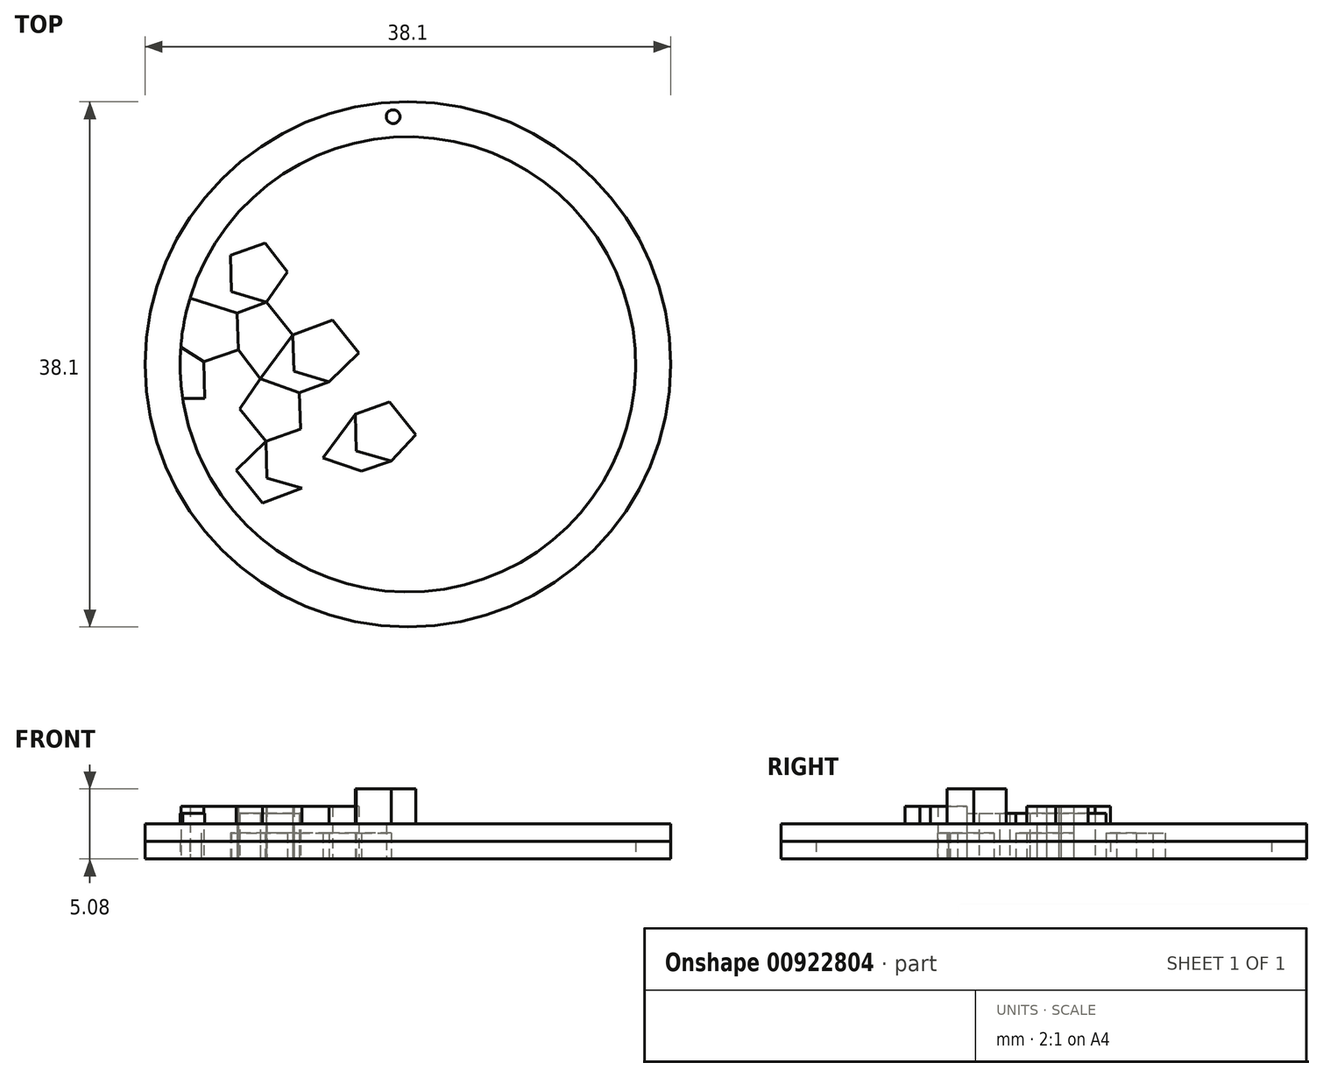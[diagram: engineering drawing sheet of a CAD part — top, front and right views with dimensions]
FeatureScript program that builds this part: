
annotation { "Feature Type Name" : "Feature", "Feature Type Description" : "" }
export const myFeature = defineFeature(function(context is Context, id is Id, definition is map)
    precondition{}
    {
        {
            var Q0;
            Q0=qCreatedBy(makeId("Top.planeOp"),FACE);
            var sketch = newSketch(context, id + "F0", { "sketchPlane" : qUnion([Q0])});
            skCircle(sketch, "E0", {"center": v(1.07, 1.9) * mm, "radius": 19.05 * mm});
            skPoint(sketch, "E0.first.point", {"position": v(-17.89, 0) * mm});
            skPoint(sketch, "E0.first.point.positionSnap0", {"position": v(-17.89, -0.57) * mm});
            skPoint(sketch, "E0.second.point", {"position": v(1.18, 20.95) * mm});
            skPoint(sketch, "E0.second.point.positionSnap0", {"position": v(1.18, 19.99) * mm});
            skPoint(sketch, "E0.third.point", {"position": v(19, -4.54) * mm});
            skCircle(sketch, "E1", {"center": v(1.07, 1.9) * mm, "radius": 16.51 * mm});
            skLineSegment(sketch, "E2.0", {"start": v(-11.37, -5.79) * mm, "end": v(-13.92, -5.03) * mm});
            skLineSegment(sketch, "E2.1", {"start": v(-13.92, -5.03) * mm, "end": v(-13.99, -2.38) * mm});
            skLineSegment(sketch, "E2.2", {"start": v(-13.99, -2.38) * mm, "end": v(-11.12, -1.32) * mm});
            skLineSegment(sketch, "E2.3", {"start": v(-11.23, 2.97) * mm, "end": v(-9.62, 0.87) * mm});
            skLineSegment(sketch, "E2.4", {"start": v(-9.22, -3.68) * mm, "end": v(-11.37, -5.79) * mm});
            skLineSegment(sketch, "E3.0", {"start": v(-9.22, -3.68) * mm, "end": v(-11.12, -1.32) * mm});
            skLineSegment(sketch, "E3.1", {"start": v(-11.23, 2.97) * mm, "end": v(-11.3, 5.63) * mm});
            skLineSegment(sketch, "E3.2", {"start": v(-11.3, 5.63) * mm, "end": v(-9.17, 6.41) * mm});
            skLineSegment(sketch, "E3.3", {"start": v(-9.17, 6.41) * mm, "end": v(-7.27, 4.05) * mm});
            skLineSegment(sketch, "E3.4", {"start": v(-7.27, 4.05) * mm, "end": v(-9.62, 0.87) * mm});
            skLineSegment(sketch, "E4.0", {"start": v(-11.12, -1.32) * mm, "end": v(-13.67, -0.57) * mm});
            skLineSegment(sketch, "E4.1", {"start": v(-13.67, -0.57) * mm, "end": v(-13.73, 2.09) * mm});
            skLineSegment(sketch, "E4.2", {"start": v(-13.73, 2.09) * mm, "end": v(-11.23, 2.97) * mm});
            skLineSegment(sketch, "E4.4", {"start": v(-9.62, 0.87) * mm, "end": v(-11.12, -1.32) * mm});
            skLineSegment(sketch, "E5.0", {"start": v(-9.62, 0.87) * mm, "end": v(-11.23, 2.97) * mm});
            skLineSegment(sketch, "E6.1.0.0", {"start": v(-4.7, -9.45) * mm, "end": v(-6.86, -11.55) * mm});
            skLineSegment(sketch, "E6.1.0.1", {"start": v(-6.86, -11.55) * mm, "end": v(-9.4, -10.8) * mm});
            skLineSegment(sketch, "E6.1.0.2", {"start": v(-9.4, -10.8) * mm, "end": v(-9.47, -8.15) * mm});
            skLineSegment(sketch, "E6.1.0.3", {"start": v(-9.47, -8.15) * mm, "end": v(-6.6, -7.09) * mm});
            skLineSegment(sketch, "E6.1.0.4", {"start": v(-4.7, -9.45) * mm, "end": v(-6.6, -7.09) * mm});
            skLineSegment(sketch, "E6.1.0.5", {"start": v(-5.1, -4.9) * mm, "end": v(-6.6, -7.09) * mm});
            skLineSegment(sketch, "E6.1.0.6", {"start": v(-6.6, -7.09) * mm, "end": v(-9.15, -6.33) * mm});
            skLineSegment(sketch, "E6.1.0.7", {"start": v(-9.15, -6.33) * mm, "end": v(-9.22, -3.68) * mm});
            skLineSegment(sketch, "E6.1.0.8", {"start": v(-9.22, -3.68) * mm, "end": v(-6.72, -2.8) * mm});
            skLineSegment(sketch, "E6.1.0.9", {"start": v(-5.1, -4.9) * mm, "end": v(-6.72, -2.8) * mm});
            skLineSegment(sketch, "E6.1.0.10", {"start": v(-6.72, -2.8) * mm, "end": v(-5.1, -4.9) * mm});
            skLineSegment(sketch, "E6.1.0.11", {"start": v(-2.75, -1.71) * mm, "end": v(-5.1, -4.9) * mm});
            skLineSegment(sketch, "E6.1.0.12", {"start": v(-4.66, 0.65) * mm, "end": v(-2.75, -1.71) * mm});
            skLineSegment(sketch, "E6.1.0.13", {"start": v(-6.79, -0.14) * mm, "end": v(-4.66, 0.65) * mm});
            skLineSegment(sketch, "E6.1.0.14", {"start": v(-6.72, -2.8) * mm, "end": v(-6.79, -0.14) * mm});
            skLineSegment(sketch, "E6.direction1", {"start": v(-13.92, -5.03) * mm, "end": v(-9.4, -10.8) * mm, "construction": true});
            skLineSegment(sketch, "E7", {"start": v(-11.37, -5.79) * mm, "end": v(-9.47, -8.15) * mm});
            skLineSegment(sketch, "E8", {"start": v(-9.62, 0.87) * mm, "end": v(-6.79, -0.14) * mm});
            skLineSegment(sketch, "E9.1.0.0", {"start": v(-4.66, 0.65) * mm, "end": v(-7.2, 1.4) * mm});
            skLineSegment(sketch, "E9.1.0.1", {"start": v(-7.2, 1.4) * mm, "end": v(-7.27, 4.05) * mm});
            skLineSegment(sketch, "E9.1.0.2", {"start": v(-7.27, 4.05) * mm, "end": v(-4.4, 5.11) * mm});
            skLineSegment(sketch, "E9.1.0.3", {"start": v(-2.5, 2.75) * mm, "end": v(-4.4, 5.11) * mm});
            skLineSegment(sketch, "E9.1.0.4", {"start": v(-2.5, 2.75) * mm, "end": v(-4.66, 0.65) * mm});
            skLineSegment(sketch, "E9.direction1", {"start": v(-9.4, -10.8) * mm, "end": v(-7.2, 1.4) * mm, "construction": true});
            skLineSegment(sketch, "E10.1.0.0", {"start": v(-2.68, -4.37) * mm, "end": v(-2.75, -1.71) * mm});
            skLineSegment(sketch, "E10.1.0.1", {"start": v(-0.14, -5.12) * mm, "end": v(-2.68, -4.37) * mm});
            skLineSegment(sketch, "E10.1.0.2", {"start": v(1.65, -3.19) * mm, "end": v(-0.14, -5.12) * mm});
            skLineSegment(sketch, "E10.1.0.3", {"start": v(-2.75, -1.71) * mm, "end": v(-0.25, -0.83) * mm});
            skLineSegment(sketch, "E10.1.0.4", {"start": v(1.65, -3.19) * mm, "end": v(-0.25, -0.83) * mm});
            skLineSegment(sketch, "E10.direction1", {"start": v(-9.4, -10.8) * mm, "end": v(-0.9, -7.3) * mm, "construction": true});
            skLineSegment(sketch, "E11.1.0.1", {"start": v(-7.67, 8.6) * mm, "end": v(-9.17, 6.41) * mm});
            skLineSegment(sketch, "E11.1.0.2", {"start": v(-7.67, 8.6) * mm, "end": v(-4.84, 7.67) * mm});
            skLineSegment(sketch, "E11.1.0.3", {"start": v(-4.4, 5.11) * mm, "end": v(-4.84, 7.67) * mm});
            skLineSegment(sketch, "E11.1.0.5", {"start": v(-9.17, 6.41) * mm, "end": v(-11.72, 7.17) * mm});
            skLineSegment(sketch, "E11.1.0.6", {"start": v(-11.72, 7.17) * mm, "end": v(-11.79, 9.82) * mm});
            skLineSegment(sketch, "E11.1.0.7", {"start": v(-11.79, 9.82) * mm, "end": v(-9.28, 10.7) * mm});
            skLineSegment(sketch, "E11.1.0.8", {"start": v(-7.67, 8.6) * mm, "end": v(-9.28, 10.7) * mm});
            skLineSegment(sketch, "E11.direction1", {"start": v(-9.22, -3.68) * mm, "end": v(-6.74, 4.77) * mm, "construction": true});
            skLineSegment(sketch, "E12.1.0.2", {"start": v(-5.1, -4.9) * mm, "end": v(-2.28, -5.83) * mm});
            skLineSegment(sketch, "E12.1.0.3", {"start": v(-2.2, -8.49) * mm, "end": v(-2.28, -5.83) * mm});
            skLineSegment(sketch, "E12.1.0.4", {"start": v(-4.7, -9.37) * mm, "end": v(-2.2, -8.49) * mm});
            skLineSegment(sketch, "E12.direction1", {"start": v(-9.22, -3.68) * mm, "end": v(15.78, -3.68) * mm, "construction": true});
            skLineSegment(sketch, "E13", {"start": v(-13.73, 2.09) * mm, "end": v(-15.4, 3.16) * mm});
            skLineSegment(sketch, "E14", {"start": v(-13.67, -0.57) * mm, "end": v(-15.26, -0.57) * mm});
            skLineSegment(sketch, "E15", {"start": v(-2.28, -5.83) * mm, "end": v(-0.14, -5.12) * mm});
            skLineSegment(sketch, "E16.direction1", {"start": v(-11.12, -1.32) * mm, "end": v(-15.9, 4.6) * mm, "construction": true});
            skLineSegment(sketch, "E17", {"start": v(-11.3, 5.63) * mm, "end": v(-14.73, 6.72) * mm});
            skLineSegment(sketch, "E18", {"start": v(-14.73, 6.72) * mm, "end": v(-11.79, 9.82) * mm});
            skLineSegment(sketch, "E19", {"start": v(-11.79, 9.82) * mm, "end": v(-13.19, 10.23) * mm});
            skSolve(sketch);
        }
        {
            var Q0;
            Q0 = qSketchRegion(id + "F0", true);
            extrude(context, id + "F1", {"entities" : qUnion([Q0]), "depth" : 2.54 * mm, "offsetDistance" : 25 * mm});
        }
        {
            var Q0;
            Q0=makeQuery(id+"F0.imprint","IMPRINT",FACE,{"disambiguationData":[TD([[makeQuery(id+"F0.imprint","IMPRINT",EDGE,{"derivedFrom":sQuery(id+"F0.wireOp",EDGE,"E9.1.0.0")}),-1.0]])]});
            var Q1;
            Q1=makeQuery(id+"F0.imprint","IMPRINT",FACE,{"disambiguationData":[TD([[makeQuery(id+"F0.imprint","IMPRINT",EDGE,{"derivedFrom":sQuery(id+"F0.wireOp",EDGE,"E3.1")}),1.0]])]});
            var Q2;
            Q2=makeQuery(id+"F0.imprint","IMPRINT",FACE,{"disambiguationData":[TD([[makeQuery(id+"F0.imprint","IMPRINT",EDGE,{"derivedFrom":sQuery(id+"F0.wireOp",EDGE,"E2.4")}),1.0]])]});
            extrude(context, id + "F2", {"entities" : qUnion([Q0, Q1, Q2]), "depth" : 3.81 * mm, "offsetDistance" : 25 * mm});
        }
        {
            var Q0;
            Q0=makeQuery(id+"F0.imprint","IMPRINT",FACE,{"disambiguationData":[TD([[makeQuery(id+"F0.imprint","IMPRINT",EDGE,{"derivedFrom":sQuery(id+"F0.wireOp",EDGE,"E3.4")}),1.0]])]});
            var Q1;
            Q1=makeQuery(id+"F0.imprint","IMPRINT",FACE,{"disambiguationData":[TD([[makeQuery(id+"F0.imprint","IMPRINT",EDGE,{"derivedFrom":sQuery(id+"F0.wireOp",EDGE,"E2.0")}),-1.0]])]});
            var Q2;
            {var subQ1=sQuery(id+"F0.wireOp",EDGE,"E11.1.0.1");Q2=makeQuery(id+"F0.imprint","IMPRINT",FACE,{"disambiguationData":[TD([[makeQuery(id+"F0.imprint","IMPRINT",EDGE,{"derivedFrom":subQ1}),-1.0]])]});}
            var Q3;
            Q3=makeQuery(id+"F0.imprint","IMPRINT",FACE,{"disambiguationData":[TD([[makeQuery(id+"F0.imprint","IMPRINT",EDGE,{"derivedFrom":sQuery(id+"F0.wireOp",EDGE,"E6.1.0.11")}),1.0]])]});
            extrude(context, id + "F3", {"entities" : qUnion([Q0, Q1, Q2, Q3]), "depth" : 1.9 * mm, "offsetDistance" : 25 * mm});
        }
        {
            var Q0;
            {var subQ1=sQuery(id+"F0.wireOp",EDGE,"E2.0");Q0=makeQuery(id+"F0.imprint","IMPRINT",FACE,{"disambiguationData":[TD([[makeQuery(id+"F0.imprint","IMPRINT",EDGE,{"derivedFrom":subQ1}),1.0]])]});}
            extrude(context, id + "F4", {"entities" : qUnion([Q0]), "depth" : 1.27 * mm, "offsetDistance" : 25 * mm});
        }
        {
            var Q0;
            Q0=makeQuery(id+"F0.imprint","IMPRINT",FACE,{"disambiguationData":[TD([[makeQuery(id+"F0.imprint","IMPRINT",EDGE,{"derivedFrom":sQuery(id+"F0.wireOp",EDGE,"E10.1.0.0")}),-1.0]])]});
            extrude(context, id + "F5", {"entities" : qUnion([Q0]), "depth" : 5.08 * mm, "offsetDistance" : 25 * mm});
        }
        {
            var Q0;
            Q0=makeQuery(id+"F0.imprint","IMPRINT",FACE,{"disambiguationData":[TD([[makeQuery(id+"F0.imprint","IMPRINT",EDGE,{"derivedFrom":sQuery(id+"F0.wireOp",EDGE,"E3.1")}),-1.0]])]});
            var Q1;
            Q1=makeQuery(id+"F0.imprint","IMPRINT",FACE,{"disambiguationData":[TD([[makeQuery(id+"F0.imprint","IMPRINT",EDGE,{"derivedFrom":sQuery(id+"F0.wireOp",EDGE,"E3.0")}),-1.0]])]});
            var Q2;
            Q2=makeQuery(id+"F0.imprint","IMPRINT",FACE,{"disambiguationData":[TD([[makeQuery(id+"F0.imprint","IMPRINT",EDGE,{"derivedFrom":sQuery(id+"F0.wireOp",EDGE,"E4.1")}),1.0]])]});
            extrude(context, id + "F6", {"entities" : qUnion([Q0, Q1, Q2]), "depth" : 3.3 * mm, "offsetDistance" : 25 * mm});
        }
        {
            var Q0;
            Q0=qCreatedBy(makeId("Top.planeOp"),FACE);
            var sketch = newSketch(context, id + "F7", { "sketchPlane" : qUnion([Q0])});
            skPoint(sketch, "E20", {"position": v(0, 19.87) * mm});
            skSolve(sketch);
        }
        {
            var Q0;
            Q0=sQuery(id+"F7.wireOp",VERTEX,"E20");
            var Q1;
            Q1=makeQuery(id+"F1.opExtrude","SWEPT_BODY",BODY,{"disambiguationData":[OSD([sQuery(id+"F0.wireOp",EDGE,"E0"),sQuery(id+"F0.wireOp",EDGE,"E1")])]});
            hole(context, id + "F8", {"style" : HoleStyle.SIMPLE, "endStyle" : HoleEndStyle.THROUGH, "oppositeDirection" : true, "holeDiameter" : 1 * mm, "majorDiameter" : 5 * mm, "isTappedThrough" : true, "tappedDepth" : 12 * mm, "tapClearance" : 3, "startFromSketch" : true, "locations" : qUnion([Q0]), "scope" : qUnion([Q1])});
        }
    });
